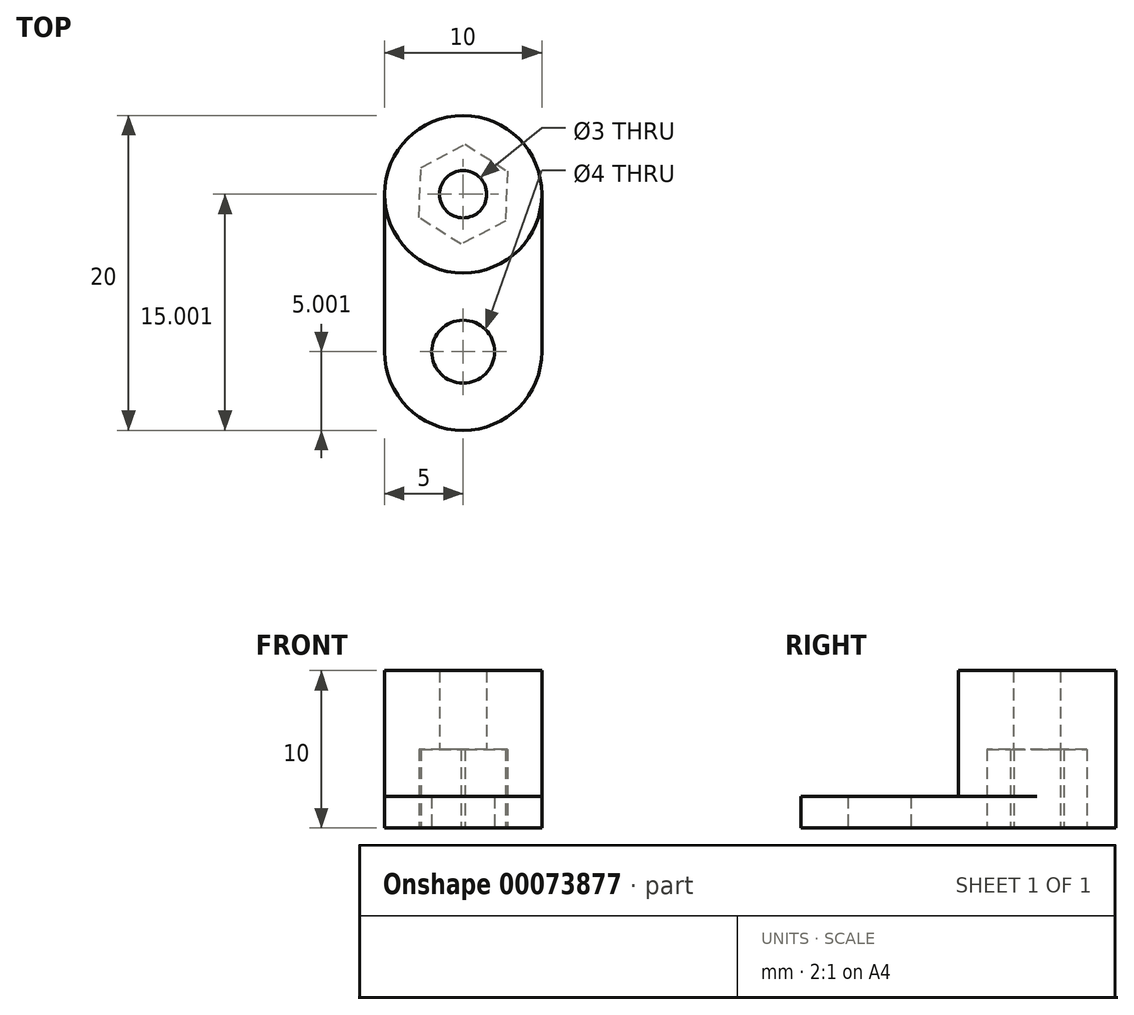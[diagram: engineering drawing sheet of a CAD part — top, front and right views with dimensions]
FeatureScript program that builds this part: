
annotation { "Feature Type Name" : "Feature", "Feature Type Description" : "" }
export const myFeature = defineFeature(function(context is Context, id is Id, definition is map)
    precondition{}
    {
        {
            var Q0;
            Q0=qCreatedBy(makeId("Top.planeOp"),FACE);
            var sketch = newSketch(context, id + "F0", { "sketchPlane" : qUnion([Q0])});
            skCircle(sketch, "E0", {"center": v(0, 7.72) * mm, "radius": 5 * mm});
            skCircle(sketch, "E1", {"center": v(0, 17.72) * mm, "radius": 5 * mm});
            skLineSegment(sketch, "E2", {"start": v(-5, 17.72) * mm, "end": v(-5, 7.72) * mm});
            skLineSegment(sketch, "E3", {"start": v(5, 17.72) * mm, "end": v(5, 7.72) * mm});
            skCircle(sketch, "E4", {"center": v(0, 17.72) * mm, "radius": 1.5 * mm});
            skCircle(sketch, "E5", {"center": v(0, 7.72) * mm, "radius": 2 * mm});
            skCircle(sketch, "E6.cCircle", {"center": v(0, 17.72) * mm, "radius": 2.75 * mm, "construction": true});
            skLineSegment(sketch, "E6.0", {"start": v(-2.68, 19.42) * mm, "end": v(0.13, 20.9) * mm});
            skLineSegment(sketch, "E6.1", {"start": v(0.13, 20.9) * mm, "end": v(2.81, 19.2) * mm});
            skLineSegment(sketch, "E6.2", {"start": v(2.81, 19.2) * mm, "end": v(2.68, 16.02) * mm});
            skLineSegment(sketch, "E6.3", {"start": v(2.68, 16.02) * mm, "end": v(-0.13, 14.55) * mm});
            skLineSegment(sketch, "E6.4", {"start": v(-0.13, 14.55) * mm, "end": v(-2.81, 16.25) * mm});
            skLineSegment(sketch, "E6.5", {"start": v(-2.81, 16.25) * mm, "end": v(-2.68, 19.42) * mm});
            skPoint(sketch, "E6.0.midPoint", {"position": v(-1.28, 20.16) * mm});
            skSolve(sketch);
        }
        {
            var Q0;
            Q0=makeQuery(id+"F0.imprint","IMPRINT",FACE,{"disambiguationData":[TD([[makeQuery(id+"F0.imprint","IMPRINT",EDGE,{"derivedFrom":sQuery(id+"F0.wireOp",EDGE,"E6.0")}),1.0]])]});
            var Q1;
            Q1=makeQuery(id+"F0.imprint","IMPRINT",FACE,{"disambiguationData":[TD([[makeQuery(id+"F0.imprint","IMPRINT",EDGE,{"derivedFrom":sQuery(id+"F0.wireOp",EDGE,"E4")}),-1.0]])]});
            extrude(context, id + "F1", {"entities" : qUnion([Q0, Q1]), "depth" : 10 * mm});
        }
        {
            var Q0;
            Q0=makeQuery(id+"F0.imprint","IMPRINT",FACE,{"disambiguationData":[TD([[makeQuery(id+"F0.imprint","IMPRINT",EDGE,{"derivedFrom":sQuery(id+"F0.wireOp",EDGE,"e7a31b72-d69c-4d1f-8b8a-69072deda09a")}),-1.0]])]});
            var Q1;
            {var subQ0=sQuery(id+"F0.wireOp",EDGE,"E3");Q1=makeQuery(id+"F0.imprint","IMPRINT",FACE,{"disambiguationData":[TD([[makeQuery(id+"F0.imprint","IMPRINT",EDGE,{"derivedFrom":subQ0}),-1.0]])]});}
            var Q2;
            Q2=makeQuery(id+"F0.imprint","IMPRINT",FACE,{"disambiguationData":[TD([[makeQuery(id+"F0.imprint","IMPRINT",EDGE,{"derivedFrom":sQuery(id+"F0.wireOp",EDGE,"E5")}),-1.0]])]});
            var Q3;
            {var subQ0=sQuery(id+"F0.wireOp",EDGE,"E2");Q3=makeQuery(id+"F0.imprint","IMPRINT",FACE,{"disambiguationData":[TD([[makeQuery(id+"F0.imprint","IMPRINT",EDGE,{"derivedFrom":subQ0}),1.0]])]});}
            extrude(context, id + "F2", {"entities" : qUnion([Q0, Q1, Q2, Q3]), "operationType" : NewBodyOperationType.ADD, "depth" : 2 * mm});
        }
        {
            var Q0;
            Q0=makeQuery(id+"F0.imprint","IMPRINT",FACE,{"disambiguationData":[TD([[makeQuery(id+"F0.imprint","IMPRINT",EDGE,{"derivedFrom":sQuery(id+"F0.wireOp",EDGE,"E4")}),-1.0]])]});
            extrude(context, id + "F3", {"entities" : qUnion([Q0]), "operationType" : NewBodyOperationType.REMOVE, "depth" : 5 * mm});
        }
    });
